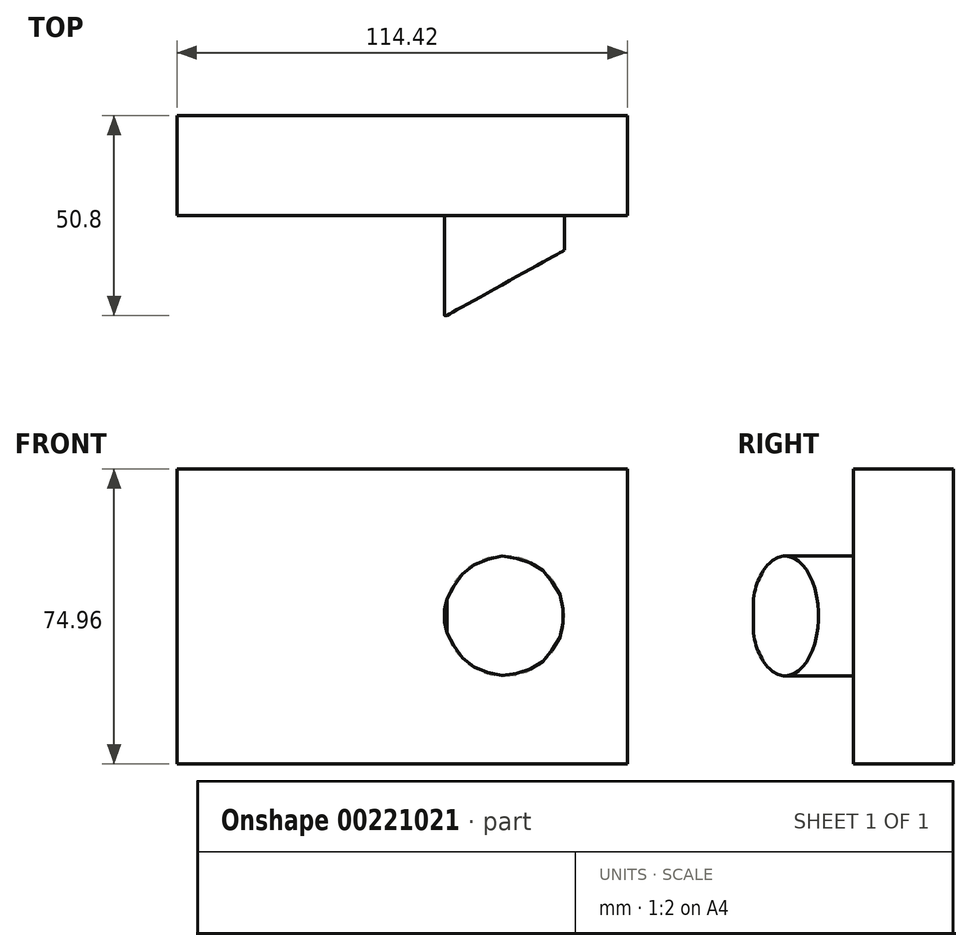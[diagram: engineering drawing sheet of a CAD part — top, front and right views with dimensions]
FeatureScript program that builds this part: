
annotation { "Feature Type Name" : "Feature", "Feature Type Description" : "" }
export const myFeature = defineFeature(function(context is Context, id is Id, definition is map)
    precondition{}
    {
        {
            var Q0;
            Q0=qCreatedBy(makeId("Front.planeOp"),FACE);
            var sketch = newSketch(context, id + "F0", { "sketchPlane" : qUnion([Q0])});
            skLineSegment(sketch, "E0.bottom", {"start": v(-52.24, 37.34) * mm, "end": v(62.18, 37.34) * mm});
            skLineSegment(sketch, "E0.top", {"start": v(-52.24, -37.62) * mm, "end": v(62.18, -37.62) * mm});
            skLineSegment(sketch, "E0.left", {"start": v(-52.24, 37.34) * mm, "end": v(-52.24, -37.62) * mm});
            skLineSegment(sketch, "E0.right", {"start": v(62.18, 37.34) * mm, "end": v(62.18, -37.62) * mm});
            skSolve(sketch);
        }
        {
            var Q0;
            Q0=makeQuery(id+"F0.imprint","IMPRINT",FACE,{"disambiguationData":[TD([[makeQuery(id+"F0.imprint","IMPRINT",EDGE,{"derivedFrom":sQuery(id+"F0.wireOp",EDGE,"E0.bottom")}),-1.0]])]});
            extrude(context, id + "F1", {"entities" : qUnion([Q0]), "depth" : 25.4 * mm});
        }
        {
            var Q0;
            Q0=makeQuery(id+"F1.opExtrude","CAP_FACE",FACE,{"disambiguationData":[OSD([sQuery(id+"F0.wireOp",EDGE,"E0.bottom"),sQuery(id+"F0.wireOp",EDGE,"E0.top"),sQuery(id+"F0.wireOp",EDGE,"E0.left"),sQuery(id+"F0.wireOp",EDGE,"E0.right")])],"isStart":false});
            var sketch = newSketch(context, id + "F2", { "sketchPlane" : qUnion([Q0])});
            skCircle(sketch, "E1", {"center": v(30.95, 0) * mm, "radius": 15.24 * mm});
            skSolve(sketch);
        }
        {
            var Q0;
            Q0 = qSketchRegion(id + "F2", true);
            extrude(context, id + "F3", {"entities" : qUnion([Q0]), "operationType" : NewBodyOperationType.ADD, "depth" : 25.4 * mm});
        }
        {
            var Q0;
            Q0=qCreatedBy(makeId("Top.planeOp"),FACE);
            var sketch = newSketch(context, id + "F4", { "sketchPlane" : qUnion([Q0])});
            skLineSegment(sketch, "E2", {"start": v(46.73, -33.92) * mm, "end": v(12.96, -52.68) * mm});
            skLineSegment(sketch, "E3", {"start": v(12.96, -52.68) * mm, "end": v(50.75, -52.68) * mm});
            skLineSegment(sketch, "E4", {"start": v(50.75, -52.68) * mm, "end": v(46.73, -33.92) * mm});
            skSolve(sketch);
        }
        {
            var Q0;
            Q0 = qSketchRegion(id + "F4", true);
            extrude(context, id + "F5", {"entities" : qUnion([Q0]), "operationType" : NewBodyOperationType.REMOVE, "endBound" : BoundingType.SYMMETRIC, "oppositeDirection" : true, "depth" : 50.8 * mm});
        }
    });
